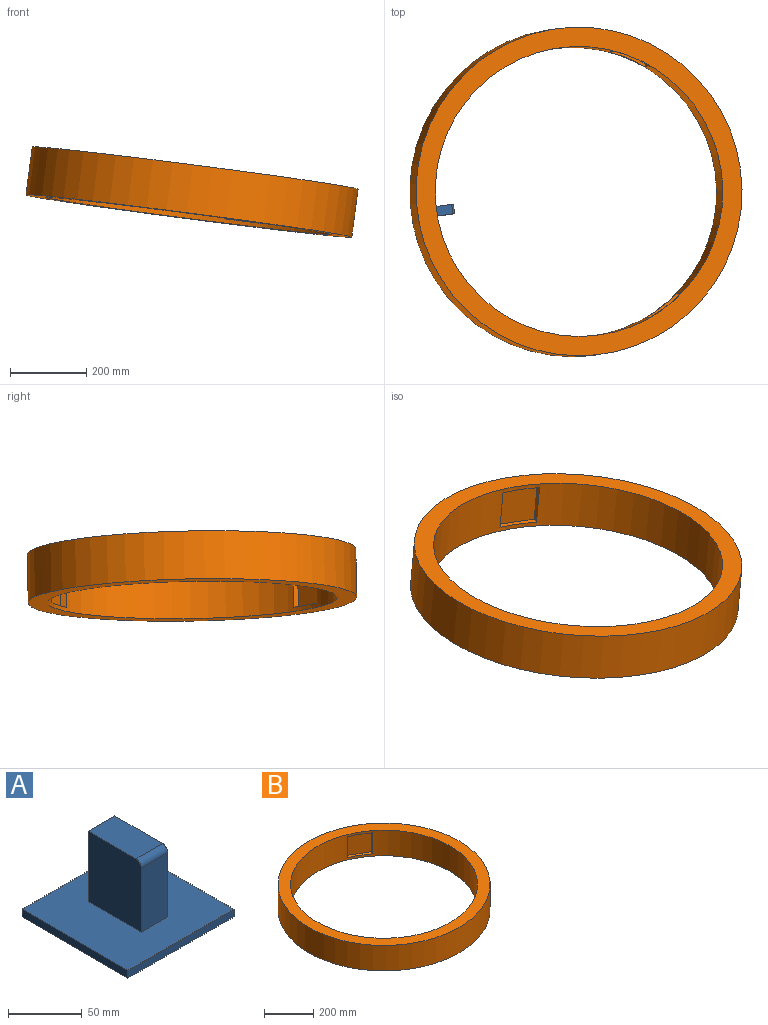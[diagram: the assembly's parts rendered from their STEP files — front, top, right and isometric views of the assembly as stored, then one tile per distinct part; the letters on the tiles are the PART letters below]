
ASSEMBLY  parts=2 mates=1
PART A: 12 faces, bbox 101.6x101.6x64.8 mm
  f0: plane 101.6x101.6mm, normal (0,0,1), area 9032.2mm2, adj f1,f2,f3,f4,f6,f7,f8,f9
  f1: plane 101.6x6.35mm, normal (0,-1,0), area 645.2mm2, adj f0,f2,f4,f5
  f2: plane 101.6x6.35mm, normal (1,0,0), area 645.2mm2, adj f0,f1,f3,f5
  f3: plane 101.6x6.35mm, normal (0,1,0), area 645.2mm2, adj f0,f2,f4,f5
  f4: plane 101.6x6.35mm, normal (-1,0,0), area 645.2mm2, adj f0,f1,f3,f5
  f5: plane 101.6x101.6mm, normal (0,0,-1), area 10322.6mm2, adj f1,f2,f3,f4
  f6: plane 53.34x25.4mm, normal (0,-1,0), area 1354.8mm2, adj f0,f7,f9,f11
  f7: plane 58.42x50.8mm, normal (1,0,0), area 2962.2mm2, adj f0,f6,f8,f10,f11
  f8: plane 58.42x25.4mm, normal (0,1,0), area 1483.9mm2, adj f0,f7,f9,f10
  f9: plane 58.42x50.8mm, normal (-1,0,0), area 2962.2mm2, adj f0,f6,f8,f10,f11
  f10: plane 45.72x25.4mm, normal (0,0,1), area 1161.3mm2, adj f7,f8,f9,f11
  f11: cylinder r=5.08mm len=25.4mm, axis (-1,0,0), area 202.7mm2, adj f6,f7,f9,f10
PART B: 19 faces, bbox 863.6x863.6x127 mm
  f0: cylinder r=381mm len=762mm, axis (0,0,-1), area 270986.4mm2, adj f2,f3,f4,f6,f7,f8,f9,f11
  f1: cylinder r=431.8mm len=863.6mm, axis (0,0,-1), area 344561.1mm2, adj f2,f3
  f2: plane 863.6x863.6mm, normal (0,0,1), area 129717.1mm2, adj f0,f1
  f3: plane 863.6x863.6mm, normal (0,0,-1), area 129717.1mm2, adj f0,f1
  f4: plane 104.78x16.32mm, normal (0,0,-1), area 1456.8mm2, adj f0,f5,f7,f8
  f5: plane 104.78x104.78mm, normal (1,0,0), area 10977.8mm2, adj f4,f6,f7,f8
  f6: plane 104.78x16.32mm, normal (0,0,1), area 1456.8mm2, adj f0,f5,f7,f8
  f7: plane 104.78x16.32mm, normal (0,-1,0), area 1709.8mm2, adj f0,f4,f5,f6
  f8: plane 104.78x16.32mm, normal (0,1,0), area 1709.8mm2, adj f0,f4,f5,f6
  f9: plane 98.9x66.52mm, normal (0,0,-1), area 1456.8mm2, adj f0,f10,f12,f13
  f10: plane 104.78x90.74mm, normal (-0.5,0.87,0), area 10977.8mm2, adj f9,f11,f12,f13
  f11: plane 98.9x66.52mm, normal (0,0,1), area 1456.8mm2, adj f0,f10,f12,f13
  f12: plane 104.78x14.13mm, normal (0.87,0.5,0), area 1709.8mm2, adj f0,f9,f10,f11
  f13: plane 104.78x14.13mm, normal (-0.87,-0.5,0), area 1709.8mm2, adj f0,f9,f10,f11
  f14: plane 98.9x66.52mm, normal (0,0,-1), area 1456.8mm2, adj f0,f15,f17,f18
  f15: plane 104.78x90.74mm, normal (-0.5,-0.87,0), area 10977.8mm2, adj f14,f16,f17,f18
  f16: plane 98.9x66.52mm, normal (0,0,1), area 1456.8mm2, adj f0,f15,f17,f18
  f17: plane 104.78x14.13mm, normal (-0.87,0.5,0), area 1709.8mm2, adj f0,f14,f15,f16
  f18: plane 104.78x14.13mm, normal (0.87,-0.5,0), area 1709.8mm2, adj f0,f14,f15,f16
PLACE A rot(axis=(-0.65,0.57,-0.5),120.3deg) t=(-14.93,33.67,46.41)mm
PLACE B rot(axis=(-0.05,0.68,0.73),10.9deg) t=(371.72,87.54,-4.63)mm
MATE fastened B.f5 <-> A.f5  axis (0.98,0.14,-0.13) through (-14.93,33.67,46.41)mm
